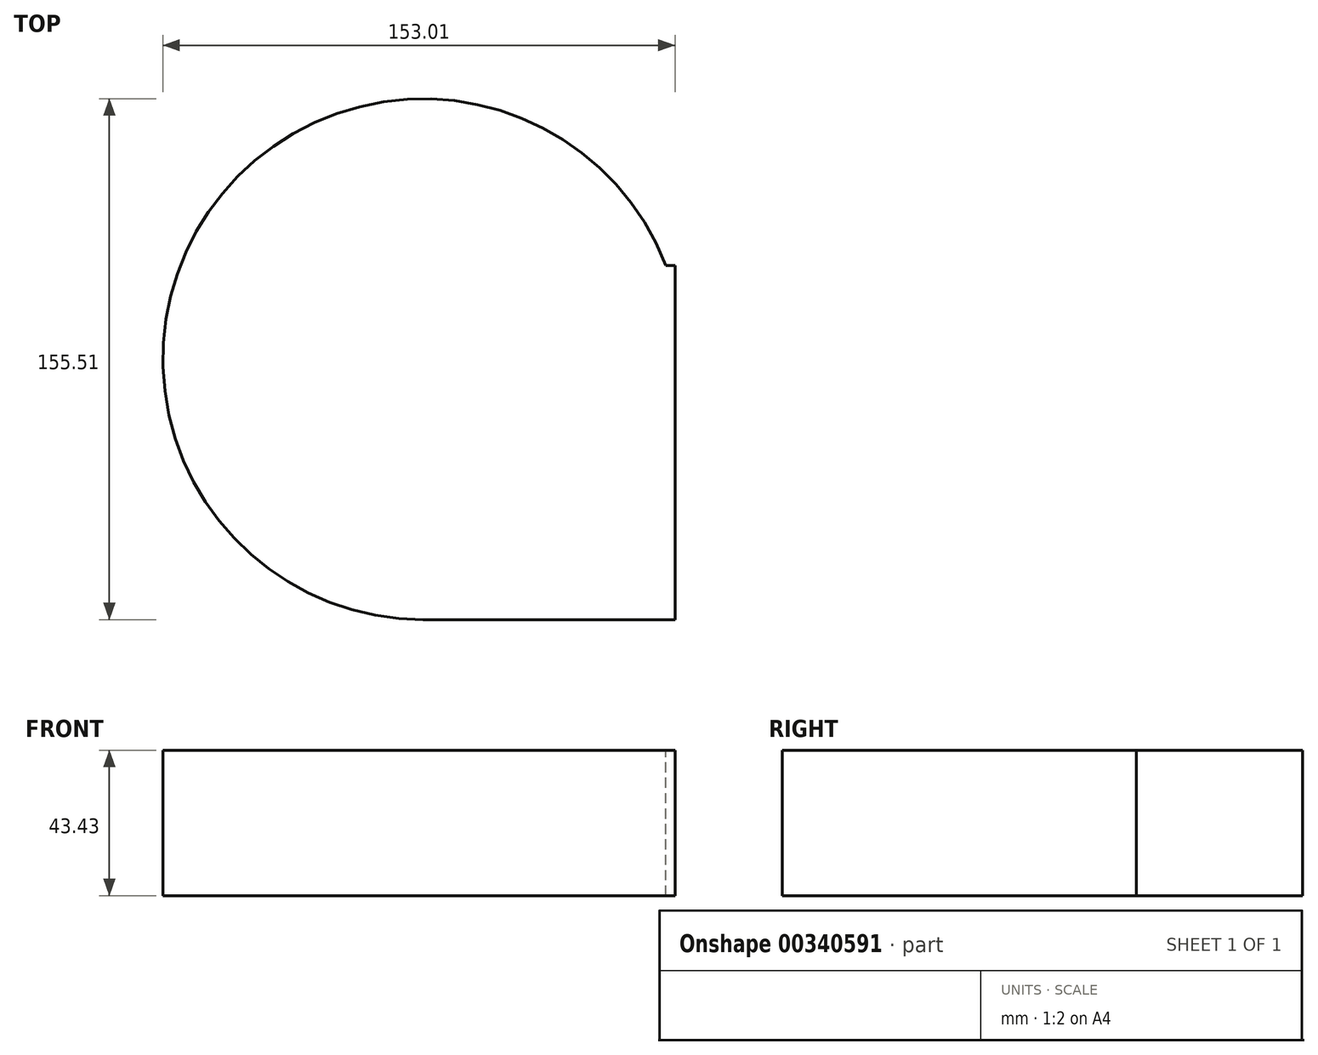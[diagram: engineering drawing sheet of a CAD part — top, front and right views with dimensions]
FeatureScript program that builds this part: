
annotation { "Feature Type Name" : "Feature", "Feature Type Description" : "" }
export const myFeature = defineFeature(function(context is Context, id is Id, definition is map)
    precondition{}
    {
        {
            var Q0;
            Q0=qCreatedBy(makeId("Top.planeOp"),FACE);
            var sketch = newSketch(context, id + "F0", { "sketchPlane" : qUnion([Q0])});
            skLineSegment(sketch, "E0.bottom", {"start": v(0, 0) * mm, "end": v(75.25, 0) * mm});
            skLineSegment(sketch, "E0.top", {"start": v(0, 38.73) * mm, "end": v(75.25, 38.73) * mm});
            skLineSegment(sketch, "E0.left", {"start": v(0, 0) * mm, "end": v(0, 38.73) * mm});
            skLineSegment(sketch, "E0.right", {"start": v(75.25, 0) * mm, "end": v(75.25, 38.73) * mm});
            skLineSegment(sketch, "E1.bottom", {"start": v(75.25, 0) * mm, "end": v(0, 0) * mm});
            skLineSegment(sketch, "E1.top", {"start": v(75.25, 38.73) * mm, "end": v(0, 38.73) * mm});
            skLineSegment(sketch, "E2.top", {"start": v(0, 47.2) * mm, "end": v(75.25, 47.2) * mm});
            skLineSegment(sketch, "E2.left", {"start": v(0, 38.73) * mm, "end": v(0, 47.2) * mm});
            skLineSegment(sketch, "E2.right", {"start": v(75.25, 38.73) * mm, "end": v(75.25, 47.2) * mm});
            skLineSegment(sketch, "E3.top", {"start": v(0, -58.6) * mm, "end": v(75.25, -58.6) * mm});
            skLineSegment(sketch, "E3.left", {"start": v(0, 0) * mm, "end": v(0, -58.6) * mm});
            skLineSegment(sketch, "E3.right", {"start": v(75.25, 0) * mm, "end": v(75.25, -58.6) * mm});
            skArc(sketch, "E4", {"start": v(0, -58.6) * mm, "mid": v(-61.51, 66.72) * mm, "end": v(75.25, 38.73) * mm});
            skSolve(sketch);
        }
        {
            var Q0;
            {var subQ0=sQuery(id+"F0.wireOp",EDGE,"E2.right");Q0=makeQuery(id+"F0.imprint","IMPRINT",FACE,{"disambiguationData":[TD([[makeQuery(id+"F0.imprint","IMPRINT",EDGE,{"derivedFrom":subQ0}),1.0]])]});}
            var Q1;
            Q1=makeQuery(id+"F0.imprint","IMPRINT",FACE,{"disambiguationData":[TD([[makeQuery(id+"F0.imprint","IMPRINT",EDGE,{"derivedFrom":sQuery(id+"F0.wireOp",EDGE,"E0.bottom")}),-1.0]])]});
            var Q2;
            Q2=makeQuery(id+"F0.imprint","IMPRINT",FACE,{"disambiguationData":[TD([[makeQuery(id+"F0.imprint","IMPRINT",EDGE,{"derivedFrom":sQuery(id+"F0.wireOp",EDGE,"E0.right")}),1.0]])]});
            var Q3;
            {var subQ0=sQuery(id+"F0.wireOp",EDGE,"E0.top");Q3=makeQuery(id+"F0.imprint","IMPRINT",FACE,{"disambiguationData":[TD([[makeQuery(id+"F0.imprint","IMPRINT",EDGE,{"derivedFrom":subQ0}),1.0]])]});}
            var Q4;
            Q4=makeQuery(id+"F0.imprint","IMPRINT",FACE,{"disambiguationData":[TD([[makeQuery(id+"F0.imprint","IMPRINT",EDGE,{"derivedFrom":sQuery(id+"F0.wireOp",EDGE,"E0.left")}),1.0]])]});
            extrude(context, id + "F1", {"entities" : qUnion([Q0, Q1, Q2, Q3, Q4]), "oppositeDirection" : true, "depth" : 68.83 * mm, "hasSecondDirection" : true, "secondDirectionOppositeDirection" : true, "secondDirectionDepth" : 25.4 * mm});
        }
    });
